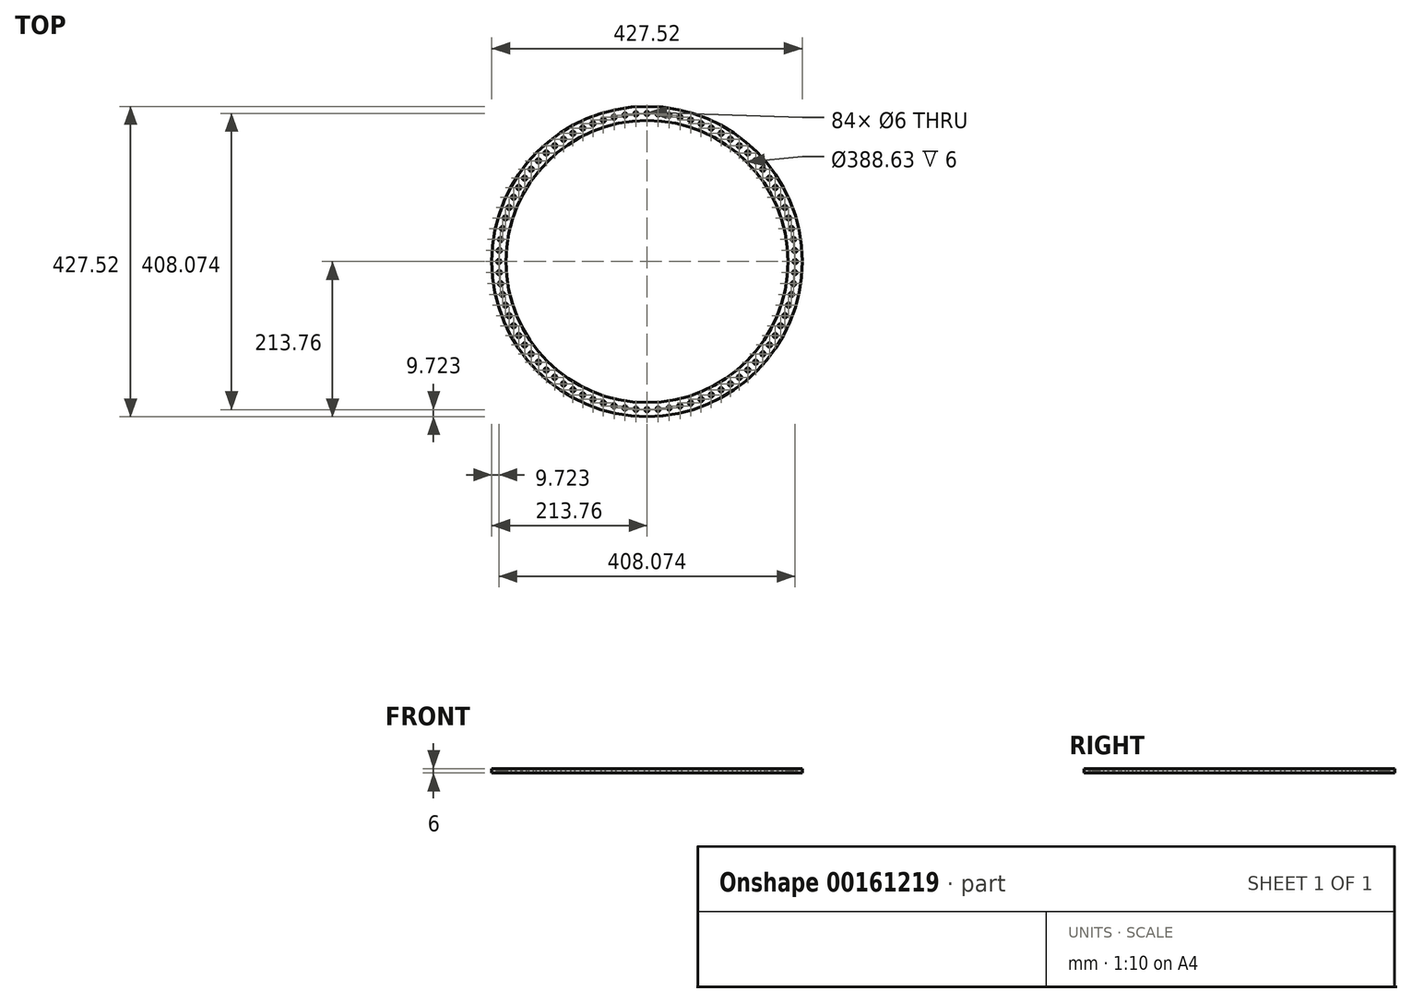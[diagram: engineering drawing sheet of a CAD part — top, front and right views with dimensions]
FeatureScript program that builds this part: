
annotation { "Feature Type Name" : "Feature", "Feature Type Description" : "" }
export const myFeature = defineFeature(function(context is Context, id is Id, definition is map)
    precondition{}
    {
        {
            var Q0;
            Q0=qCreatedBy(makeId("Top.planeOp"),FACE);
            var sketch = newSketch(context, id + "F0", { "sketchPlane" : qUnion([Q0])});
            skCircle(sketch, "E0", {"center": v(0, 0) * mm, "radius": 213.76 * mm});
            skCircle(sketch, "E1", {"center": v(0, 0) * mm, "radius": 194.32 * mm});
            skSolve(sketch);
        }
        {
            var Q0;
            Q0 = qSketchRegion(id + "F0", true);
            extrude(context, id + "F1", {"entities" : qUnion([Q0]), "depth" : 6 * mm});
        }
        {
            var Q0;
            Q0=makeQuery(id+"F1.opExtrude","CAP_FACE",FACE,{"disambiguationData":[OSD([sQuery(id+"F0.wireOp",EDGE,"E0"),sQuery(id+"F0.wireOp",EDGE,"E1")])],"isStart":false});
            var sketch = newSketch(context, id + "F2", { "sketchPlane" : qUnion([Q0])});
            skLineSegment(sketch, "E2", {"start": v(0, 194.32) * mm, "end": v(0, 204.04) * mm, "construction": true});
            skCircle(sketch, "E3", {"center": v(0, 204.04) * mm, "radius": 3 * mm});
            skCircle(sketch, "E4.1.0", {"center": v(-15.25, 203.47) * mm, "radius": 3 * mm});
            skCircle(sketch, "E4.2.0", {"center": v(-30.41, 201.76) * mm, "radius": 3 * mm});
            skCircle(sketch, "E4.3.0", {"center": v(-45.4, 198.92) * mm, "radius": 3 * mm});
            skCircle(sketch, "E4.4.0", {"center": v(-60.14, 194.97) * mm, "radius": 3 * mm});
            skCircle(sketch, "E4.5.0", {"center": v(-74.54, 189.93) * mm, "radius": 3 * mm});
            skCircle(sketch, "E4.6.0", {"center": v(-88.53, 183.83) * mm, "radius": 3 * mm});
            skCircle(sketch, "E4.7.0", {"center": v(-102.02, 176.7) * mm, "radius": 3 * mm});
            skCircle(sketch, "E4.8.0", {"center": v(-114.94, 168.58) * mm, "radius": 3 * mm});
            skCircle(sketch, "E4.9.0", {"center": v(-127.21, 159.52) * mm, "radius": 3 * mm});
            skCircle(sketch, "E4.10.0", {"center": v(-138.78, 149.57) * mm, "radius": 3 * mm});
            skCircle(sketch, "E4.11.0", {"center": v(-149.57, 138.78) * mm, "radius": 3 * mm});
            skCircle(sketch, "E4.12.0", {"center": v(-159.52, 127.21) * mm, "radius": 3 * mm});
            skCircle(sketch, "E4.13.0", {"center": v(-168.58, 114.94) * mm, "radius": 3 * mm});
            skCircle(sketch, "E4.14.0", {"center": v(-176.7, 102.02) * mm, "radius": 3 * mm});
            skCircle(sketch, "E4.15.0", {"center": v(-183.83, 88.53) * mm, "radius": 3 * mm});
            skCircle(sketch, "E4.16.0", {"center": v(-189.93, 74.54) * mm, "radius": 3 * mm});
            skCircle(sketch, "E4.17.0", {"center": v(-194.97, 60.14) * mm, "radius": 3 * mm});
            skCircle(sketch, "E4.18.0", {"center": v(-198.92, 45.4) * mm, "radius": 3 * mm});
            skCircle(sketch, "E4.19.0", {"center": v(-201.76, 30.41) * mm, "radius": 3 * mm});
            skCircle(sketch, "E4.20.0", {"center": v(-203.47, 15.25) * mm, "radius": 3 * mm});
            skCircle(sketch, "E4.21.0", {"center": v(-204.04, 0) * mm, "radius": 3 * mm});
            skCircle(sketch, "E4.22.0", {"center": v(-203.47, -15.25) * mm, "radius": 3 * mm});
            skCircle(sketch, "E4.23.0", {"center": v(-201.76, -30.41) * mm, "radius": 3 * mm});
            skCircle(sketch, "E4.24.0", {"center": v(-198.92, -45.4) * mm, "radius": 3 * mm});
            skCircle(sketch, "E4.25.0", {"center": v(-194.97, -60.14) * mm, "radius": 3 * mm});
            skCircle(sketch, "E4.26.0", {"center": v(-189.93, -74.54) * mm, "radius": 3 * mm});
            skCircle(sketch, "E4.27.0", {"center": v(-183.83, -88.53) * mm, "radius": 3 * mm});
            skCircle(sketch, "E4.28.0", {"center": v(-176.7, -102.02) * mm, "radius": 3 * mm});
            skCircle(sketch, "E4.29.0", {"center": v(-168.58, -114.94) * mm, "radius": 3 * mm});
            skCircle(sketch, "E4.30.0", {"center": v(-159.52, -127.21) * mm, "radius": 3 * mm});
            skCircle(sketch, "E4.31.0", {"center": v(-149.57, -138.78) * mm, "radius": 3 * mm});
            skCircle(sketch, "E4.32.0", {"center": v(-138.78, -149.57) * mm, "radius": 3 * mm});
            skCircle(sketch, "E4.33.0", {"center": v(-127.21, -159.52) * mm, "radius": 3 * mm});
            skCircle(sketch, "E4.34.0", {"center": v(-114.94, -168.58) * mm, "radius": 3 * mm});
            skCircle(sketch, "E4.35.0", {"center": v(-102.02, -176.7) * mm, "radius": 3 * mm});
            skCircle(sketch, "E4.36.0", {"center": v(-88.53, -183.83) * mm, "radius": 3 * mm});
            skCircle(sketch, "E4.37.0", {"center": v(-74.54, -189.93) * mm, "radius": 3 * mm});
            skCircle(sketch, "E4.38.0", {"center": v(-60.14, -194.97) * mm, "radius": 3 * mm});
            skCircle(sketch, "E4.39.0", {"center": v(-45.4, -198.92) * mm, "radius": 3 * mm});
            skCircle(sketch, "E4.40.0", {"center": v(-30.41, -201.76) * mm, "radius": 3 * mm});
            skCircle(sketch, "E4.41.0", {"center": v(-15.25, -203.47) * mm, "radius": 3 * mm});
            skCircle(sketch, "E4.42.0", {"center": v(0, -204.04) * mm, "radius": 3 * mm});
            skCircle(sketch, "E4.43.0", {"center": v(15.25, -203.47) * mm, "radius": 3 * mm});
            skCircle(sketch, "E4.44.0", {"center": v(30.41, -201.76) * mm, "radius": 3 * mm});
            skCircle(sketch, "E4.45.0", {"center": v(45.4, -198.92) * mm, "radius": 3 * mm});
            skCircle(sketch, "E4.46.0", {"center": v(60.14, -194.97) * mm, "radius": 3 * mm});
            skCircle(sketch, "E4.47.0", {"center": v(74.54, -189.93) * mm, "radius": 3 * mm});
            skCircle(sketch, "E4.48.0", {"center": v(88.53, -183.83) * mm, "radius": 3 * mm});
            skCircle(sketch, "E4.49.0", {"center": v(102.02, -176.7) * mm, "radius": 3 * mm});
            skCircle(sketch, "E4.50.0", {"center": v(114.94, -168.58) * mm, "radius": 3 * mm});
            skCircle(sketch, "E4.51.0", {"center": v(127.21, -159.52) * mm, "radius": 3 * mm});
            skCircle(sketch, "E4.52.0", {"center": v(138.78, -149.57) * mm, "radius": 3 * mm});
            skCircle(sketch, "E4.53.0", {"center": v(149.57, -138.78) * mm, "radius": 3 * mm});
            skCircle(sketch, "E4.54.0", {"center": v(159.52, -127.21) * mm, "radius": 3 * mm});
            skCircle(sketch, "E4.55.0", {"center": v(168.58, -114.94) * mm, "radius": 3 * mm});
            skCircle(sketch, "E4.56.0", {"center": v(176.7, -102.02) * mm, "radius": 3 * mm});
            skCircle(sketch, "E4.57.0", {"center": v(183.83, -88.53) * mm, "radius": 3 * mm});
            skCircle(sketch, "E4.58.0", {"center": v(189.93, -74.54) * mm, "radius": 3 * mm});
            skCircle(sketch, "E4.59.0", {"center": v(194.97, -60.14) * mm, "radius": 3 * mm});
            skCircle(sketch, "E4.60.0", {"center": v(198.92, -45.4) * mm, "radius": 3 * mm});
            skCircle(sketch, "E4.61.0", {"center": v(201.76, -30.41) * mm, "radius": 3 * mm});
            skCircle(sketch, "E4.62.0", {"center": v(203.47, -15.25) * mm, "radius": 3 * mm});
            skCircle(sketch, "E4.63.0", {"center": v(204.04, 0) * mm, "radius": 3 * mm});
            skCircle(sketch, "E4.64.0", {"center": v(203.47, 15.25) * mm, "radius": 3 * mm});
            skCircle(sketch, "E4.65.0", {"center": v(201.76, 30.41) * mm, "radius": 3 * mm});
            skCircle(sketch, "E4.66.0", {"center": v(198.92, 45.4) * mm, "radius": 3 * mm});
            skCircle(sketch, "E4.67.0", {"center": v(194.97, 60.14) * mm, "radius": 3 * mm});
            skCircle(sketch, "E4.68.0", {"center": v(189.93, 74.54) * mm, "radius": 3 * mm});
            skCircle(sketch, "E4.69.0", {"center": v(183.83, 88.53) * mm, "radius": 3 * mm});
            skCircle(sketch, "E4.70.0", {"center": v(176.7, 102.02) * mm, "radius": 3 * mm});
            skCircle(sketch, "E4.71.0", {"center": v(168.58, 114.94) * mm, "radius": 3 * mm});
            skCircle(sketch, "E4.72.0", {"center": v(159.52, 127.21) * mm, "radius": 3 * mm});
            skCircle(sketch, "E4.73.0", {"center": v(149.57, 138.78) * mm, "radius": 3 * mm});
            skCircle(sketch, "E4.74.0", {"center": v(138.78, 149.57) * mm, "radius": 3 * mm});
            skCircle(sketch, "E4.75.0", {"center": v(127.21, 159.52) * mm, "radius": 3 * mm});
            skCircle(sketch, "E4.76.0", {"center": v(114.94, 168.58) * mm, "radius": 3 * mm});
            skCircle(sketch, "E4.77.0", {"center": v(102.02, 176.7) * mm, "radius": 3 * mm});
            skCircle(sketch, "E4.78.0", {"center": v(88.53, 183.83) * mm, "radius": 3 * mm});
            skCircle(sketch, "E4.79.0", {"center": v(74.54, 189.93) * mm, "radius": 3 * mm});
            skCircle(sketch, "E4.80.0", {"center": v(60.14, 194.97) * mm, "radius": 3 * mm});
            skCircle(sketch, "E4.81.0", {"center": v(45.4, 198.92) * mm, "radius": 3 * mm});
            skCircle(sketch, "E4.82.0", {"center": v(30.41, 201.76) * mm, "radius": 3 * mm});
            skCircle(sketch, "E4.83.0", {"center": v(15.25, 203.47) * mm, "radius": 3 * mm});
            skPoint(sketch, "E4.center", {"position": v(0, 0) * mm});
            skPoint(sketch, "E5", {"position": v(0, 194.32) * mm});
            skLineSegment(sketch, "E6", {"start": v(0, 0) * mm, "end": v(0, 194.32) * mm});
            skLineSegment(sketch, "E7", {"start": v(-0.32, 0.72) * mm, "end": v(15.25, 203.47) * mm});
            skPoint(sketch, "E8.1.0", {"position": v(7.44, 194.17) * mm});
            skLineSegment(sketch, "E8.anchor1", {"start": v(0, 0) * mm, "end": v(0, 194.32) * mm, "construction": true});
            skLineSegment(sketch, "E8.anchor2", {"start": v(0, 0) * mm, "end": v(7.44, 194.17) * mm, "construction": true});
            skSolve(sketch);
        }
        {
            var Q0;
            Q0 = qSketchRegion(id + "F2", true);
            extrude(context, id + "F3", {"entities" : qUnion([Q0]), "operationType" : NewBodyOperationType.REMOVE, "endBound" : BoundingType.THROUGH_ALL, "oppositeDirection" : true, "depth" : 25 * mm});
        }
    });
